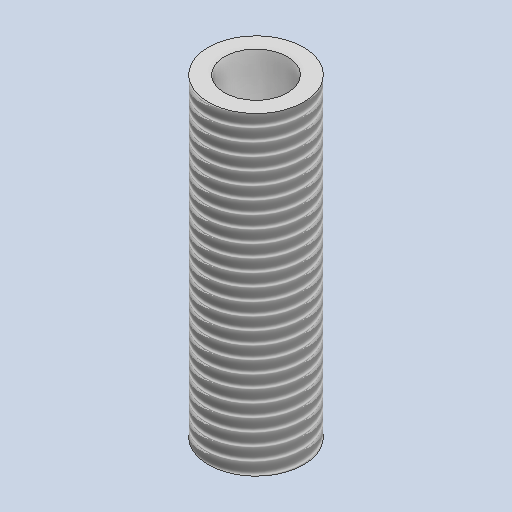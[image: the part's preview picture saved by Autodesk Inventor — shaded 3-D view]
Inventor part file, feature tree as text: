
AUTODESK INVENTOR PART (.ipt)
format: ipt  version: 2024 (Build 280153000, 153)  size: 157,184 bytes
history: native  units: mm
features: other x4, sketch x2
ambient origin geometry x8: Origin, YZ Plane, XZ Plane, XY Plane, X Axis, Y Axis, Z Axis, Center Point
bodies: Body1 (feature_tree)
feature tree (6):
  other  "TORNILLO_B.ipt"
  other  "Sólido1::TORNILLO_B.ipt"
  other  "OperaciónIdentificador1"
  sketch  "Boceto1"  dims[d0=10.0mm]
  sketch  "Boceto2"
  other  "Sólido1"
